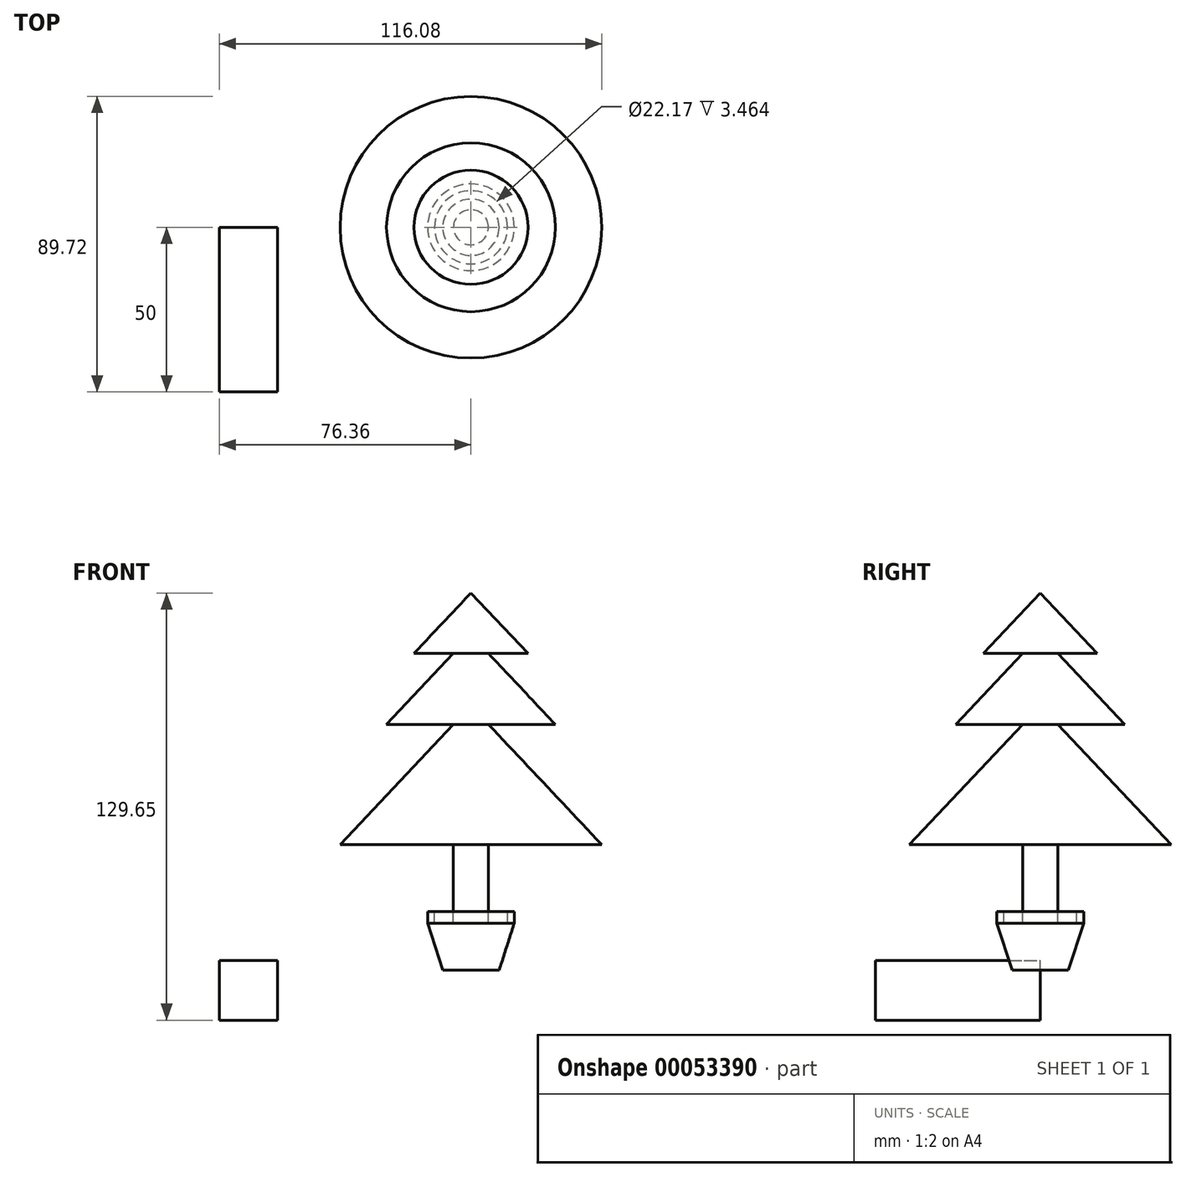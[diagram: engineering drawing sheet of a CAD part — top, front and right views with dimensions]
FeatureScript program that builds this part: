
annotation { "Feature Type Name" : "Feature", "Feature Type Description" : "" }
export const myFeature = defineFeature(function(context is Context, id is Id, definition is map)
    precondition{}
    {
        {
            var Q0;
            Q0=qCreatedBy(makeId("Front.planeOp"),FACE);
            var sketch = newSketch(context, id + "F0", { "sketchPlane" : qUnion([Q0])});
            skLineSegment(sketch, "E0", {"start": v(0, 19.74) * mm, "end": v(0, -60.61) * mm});
            skLineSegment(sketch, "E1", {"start": v(5.31, -46.3) * mm, "end": v(5.31, -30.83) * mm});
            skPoint(sketch, "E2.orphan", {"position": v(0, 63.85) * mm});
            skLineSegment(sketch, "E3", {"start": v(0, -60.61) * mm, "end": v(8.54, -60.61) * mm});
            skLineSegment(sketch, "E4", {"start": v(8.54, -60.61) * mm, "end": v(13.16, -46.3) * mm});
            skLineSegment(sketch, "E5", {"start": v(13.16, -46.3) * mm, "end": v(13.16, -42.83) * mm});
            skLineSegment(sketch, "E6", {"start": v(13.16, -42.83) * mm, "end": v(11.08, -42.83) * mm});
            skLineSegment(sketch, "E7", {"start": v(11.08, -42.83) * mm, "end": v(11.08, -46.3) * mm});
            skLineSegment(sketch, "E8", {"start": v(11.08, -46.3) * mm, "end": v(5.31, -46.3) * mm});
            skLineSegment(sketch, "E9", {"start": v(5.31, -30.83) * mm, "end": v(5.31, -22.51) * mm});
            skLineSegment(sketch, "E10", {"start": v(5.31, -22.51) * mm, "end": v(39.72, -22.51) * mm});
            skLineSegment(sketch, "E11", {"start": v(39.72, -22.51) * mm, "end": v(5.31, 13.97) * mm});
            skLineSegment(sketch, "E12", {"start": v(5.31, 13.97) * mm, "end": v(25.63, 13.97) * mm});
            skLineSegment(sketch, "E13", {"start": v(25.63, 13.97) * mm, "end": v(5.31, 35.52) * mm});
            skLineSegment(sketch, "E14", {"start": v(5.31, 35.52) * mm, "end": v(17.32, 35.52) * mm});
            skLineSegment(sketch, "E15", {"start": v(17.32, 35.52) * mm, "end": v(0, 53.88) * mm});
            skLineSegment(sketch, "E16", {"start": v(0, 53.88) * mm, "end": v(0, 19.74) * mm});
            skSolve(sketch);
        }
        {
            var Q0;
            Q0=makeQuery(id+"F0.imprint","IMPRINT",FACE,{"disambiguationData":[TD([[makeQuery(id+"F0.imprint","IMPRINT",EDGE,{"derivedFrom":sQuery(id+"F0.wireOp",EDGE,"E0")}),1.0]])]});
            var Q1;
            Q1=sQuery(id+"F0.wireOp",EDGE,"E0");
            revolve(context, id + "F1", {"entities" : qUnion([Q0]), "axis" : qUnion([Q1]), "revolveType" : RevolveType.FULL});
        }
        {
            var Q0;
            Q0=qCreatedBy(makeId("Front.planeOp"),FACE);
            var sketch = newSketch(context, id + "F2", { "sketchPlane" : qUnion([Q0])});
            skLineSegment(sketch, "E17.bottom", {"start": v(-76.36, -75.77) * mm, "end": v(-58.7, -75.77) * mm});
            skLineSegment(sketch, "E17.top", {"start": v(-76.36, -57.68) * mm, "end": v(-58.7, -57.68) * mm});
            skLineSegment(sketch, "E17.left", {"start": v(-76.36, -75.77) * mm, "end": v(-76.36, -57.68) * mm});
            skLineSegment(sketch, "E17.right", {"start": v(-58.7, -75.77) * mm, "end": v(-58.7, -57.68) * mm});
            skSolve(sketch);
        }
        {
            var Q0;
            Q0 = qSketchRegion(id + "F2", true);
            extrude(context, id + "F3", {"entities" : qUnion([Q0]), "depth" : 50 * mm});
        }
    });
